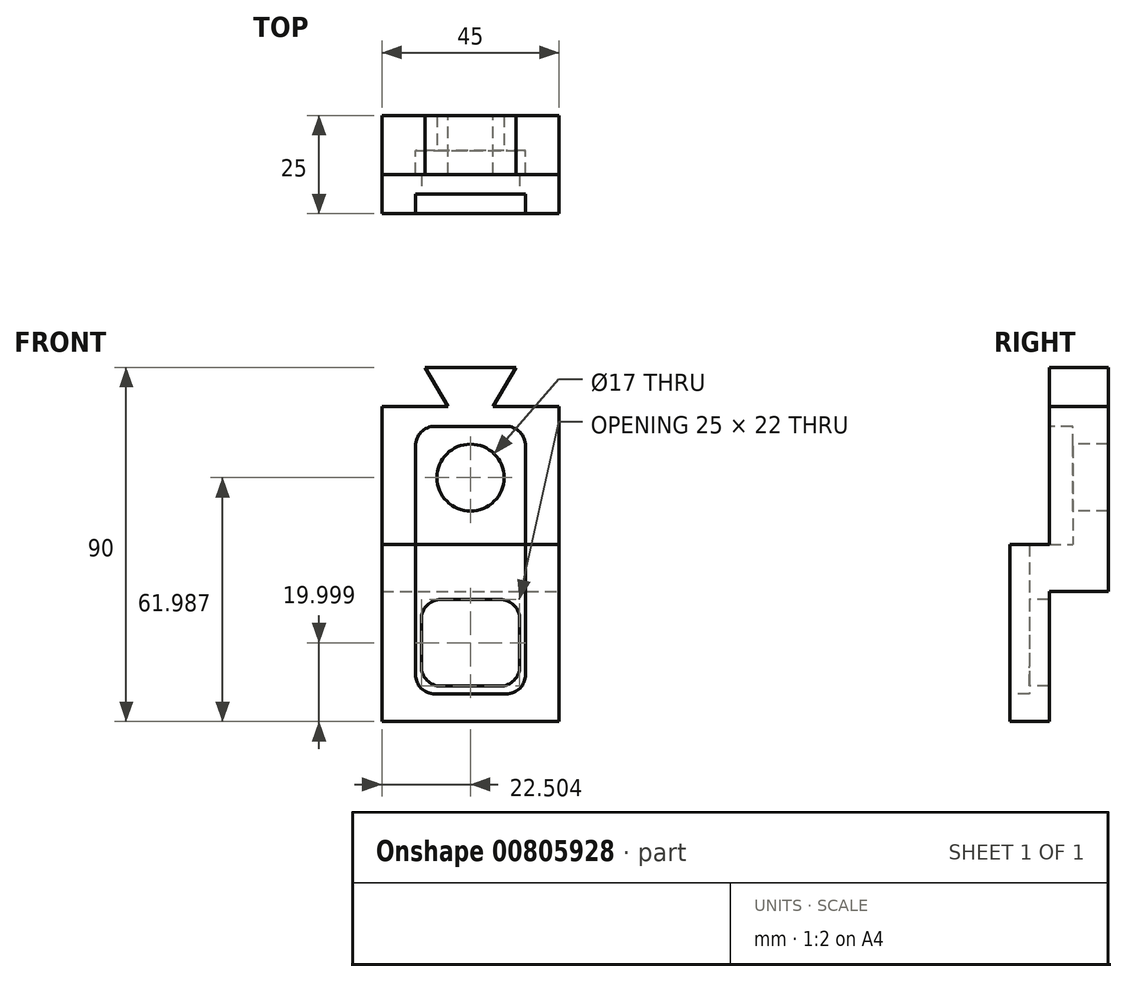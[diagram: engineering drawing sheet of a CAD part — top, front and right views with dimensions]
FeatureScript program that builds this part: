
annotation { "Feature Type Name" : "Feature", "Feature Type Description" : "" }
export const myFeature = defineFeature(function(context is Context, id is Id, definition is map)
    precondition{}
    {
        {
            var Q0;
            Q0=qCreatedBy(makeId("Front.planeOp"),FACE);
            var sketch = newSketch(context, id + "F0", { "sketchPlane" : qUnion([Q0])});
            skLineSegment(sketch, "E0.bottom", {"start": v(-9.42, 1.72) * mm, "end": v(13.58, 1.72) * mm});
            skLineSegment(sketch, "E1", {"start": v(-9.42, 1.72) * mm, "end": v(-3.64, -8.28) * mm});
            skLineSegment(sketch, "E2", {"start": v(7.81, -8.28) * mm, "end": v(13.58, 1.72) * mm});
            skLineSegment(sketch, "E3.bottom", {"start": v(-20.42, -8.28) * mm, "end": v(-3.64, -8.28) * mm});
            skLineSegment(sketch, "E3.top", {"start": v(-20.42, -58.28) * mm, "end": v(24.58, -58.28) * mm});
            skLineSegment(sketch, "E3.left", {"start": v(-20.42, -8.28) * mm, "end": v(-20.42, -58.28) * mm});
            skLineSegment(sketch, "E3.right", {"start": v(24.58, -8.28) * mm, "end": v(24.58, -58.28) * mm});
            skPoint(sketch, "E4.startSnap0", {"position": v(2.08, 1.72) * mm});
            skPoint(sketch, "E4.start.orphan", {"position": v(2.08, 7.05) * mm});
            skLineSegment(sketch, "E5.trimOffspring", {"start": v(7.81, -8.28) * mm, "end": v(24.58, -8.28) * mm});
            skSolve(sketch);
        }
        {
            var Q0;
            Q0=makeQuery(id+"F0.imprint","IMPRINT",FACE,{"disambiguationData":[TD([[makeQuery(id+"F0.imprint","IMPRINT",EDGE,{"derivedFrom":sQuery(id+"F0.wireOp",EDGE,"E0.bottom")}),-1.0]])]});
            extrude(context, id + "F1", {"entities" : qUnion([Q0]), "depth" : 25 * mm, "offsetDistance" : 25 * mm});
        }
        {
            var Q0;
            Q0=makeQuery(id+"F1.opExtrude","CAP_FACE",FACE,{"disambiguationData":[OSD([sQuery(id+"F0.wireOp",EDGE,"E0.bottom"),sQuery(id+"F0.wireOp",EDGE,"E1"),sQuery(id+"F0.wireOp",EDGE,"E2"),sQuery(id+"F0.wireOp",EDGE,"E3.bottom"),sQuery(id+"F0.wireOp",EDGE,"E3.top"),sQuery(id+"F0.wireOp",EDGE,"E3.left"),sQuery(id+"F0.wireOp",EDGE,"E3.right"),sQuery(id+"F0.wireOp",EDGE,"E5.trimOffspring")])],"isStart":false});
            var sketch = newSketch(context, id + "F2", { "sketchPlane" : qUnion([Q0])});
            skCircle(sketch, "E6", {"center": v(2.08, -26.3) * mm, "radius": 8.5 * mm});
            skPoint(sketch, "E6.centerSnap0", {"position": v(2.08, 1.72) * mm});
            skSolve(sketch);
        }
        {
            var Q0;
            Q0=makeQuery(id+"F2.imprint","IMPRINT",FACE,{"disambiguationData":[TD([[makeQuery(id+"F2.imprint","IMPRINT",EDGE,{"derivedFrom":sQuery(id+"F2.wireOp",EDGE,"E6")}),1.0]])]});
            extrude(context, id + "F3", {"entities" : qUnion([Q0]), "operationType" : NewBodyOperationType.REMOVE, "oppositeDirection" : true, "depth" : 25 * mm, "offsetDistance" : 25 * mm});
        }
        {
            var Q0;
            Q0=makeQuery(id+"F1.opExtrude","CAP_FACE",FACE,{"disambiguationData":[OSD([sQuery(id+"F0.wireOp",EDGE,"E0.bottom"),sQuery(id+"F0.wireOp",EDGE,"E1"),sQuery(id+"F0.wireOp",EDGE,"E2"),sQuery(id+"F0.wireOp",EDGE,"E3.bottom"),sQuery(id+"F0.wireOp",EDGE,"E3.top"),sQuery(id+"F0.wireOp",EDGE,"E3.left"),sQuery(id+"F0.wireOp",EDGE,"E3.right"),sQuery(id+"F0.wireOp",EDGE,"E5.trimOffspring")])],"isStart":false});
            var sketch = newSketch(context, id + "F4", { "sketchPlane" : qUnion([Q0])});
            skLineSegment(sketch, "E7.bottom", {"start": v(-6.92, -13.28) * mm, "end": v(11.08, -13.28) * mm});
            skLineSegment(sketch, "E7.top", {"start": v(-11.92, -58.28) * mm, "end": v(16.08, -58.28) * mm});
            skLineSegment(sketch, "E7.left", {"start": v(-11.92, -18.28) * mm, "end": v(-11.92, -58.28) * mm});
            skLineSegment(sketch, "E7.right", {"start": v(16.08, -18.28) * mm, "end": v(16.08, -58.28) * mm});
            skPoint(sketch, "E8.visualSharp", {"position": v(-11.92, -13.28) * mm});
            skArc(sketch, "E8.filletArc", {"start": v(-6.92, -13.28) * mm, "mid": v(-10.45, -14.75) * mm, "end": v(-11.92, -18.28) * mm});
            skPoint(sketch, "E9.visualSharp", {"position": v(16.08, -13.28) * mm});
            skArc(sketch, "E9.filletArc", {"start": v(16.08, -18.28) * mm, "mid": v(14.62, -14.75) * mm, "end": v(11.08, -13.28) * mm});
            skSolve(sketch);
        }
        {
            var Q0;
            Q0 = qSketchRegion(id + "F4", true);
            extrude(context, id + "F5", {"entities" : qUnion([Q0]), "operationType" : NewBodyOperationType.REMOVE, "oppositeDirection" : true, "depth" : 6 * mm, "offsetDistance" : 25 * mm});
        }
        {
            var Q0;
            Q0=makeQuery(id+"F5.boolean.opBoolean","COPY",FACE,{"derivedFrom":makeQuery(id+"F5.opExtrude","CAP_FACE",FACE,{"disambiguationData":[OSD([sQuery(id+"F4.wireOp",EDGE,"E7.bottom"),sQuery(id+"F4.wireOp",EDGE,"E7.top"),sQuery(id+"F4.wireOp",EDGE,"E7.left"),sQuery(id+"F4.wireOp",EDGE,"E7.right"),sQuery(id+"F4.wireOp",EDGE,"E8.filletArc"),sQuery(id+"F4.wireOp",EDGE,"E9.filletArc")])],"isStart":false})});
            var sketch = newSketch(context, id + "F6", { "sketchPlane" : qUnion([Q0])});
            skLineSegment(sketch, "E10.bottom", {"start": v(-11.92, -43.28) * mm, "end": v(16.08, -43.28) * mm});
            skLineSegment(sketch, "E10.top", {"start": v(-11.92, -58.28) * mm, "end": v(16.08, -58.28) * mm});
            skLineSegment(sketch, "E10.left", {"start": v(-11.92, -43.28) * mm, "end": v(-11.92, -58.28) * mm});
            skLineSegment(sketch, "E10.right", {"start": v(16.08, -43.28) * mm, "end": v(16.08, -58.28) * mm});
            skSolve(sketch);
        }
        {
            var Q0;
            Q0=makeQuery(id+"F6.imprint","IMPRINT",FACE,{"disambiguationData":[TD([[makeQuery(id+"F6.imprint","IMPRINT",EDGE,{"derivedFrom":sQuery(id+"F6.wireOp",EDGE,"E10.bottom")}),-1.0]])]});
            extrude(context, id + "F7", {"entities" : qUnion([Q0]), "operationType" : NewBodyOperationType.ADD, "depth" : 6 * mm, "offsetDistance" : 25 * mm});
        }
        {
            var Q0;
            Q0=makeQuery(id+"F7.boolean.opBoolean","MERGE",FACE,{"derivedFrom":[makeQuery(id+"F1.opExtrude","CAP_FACE",FACE,{"disambiguationData":[OSD([sQuery(id+"F0.wireOp",EDGE,"E0.bottom"),sQuery(id+"F0.wireOp",EDGE,"E1"),sQuery(id+"F0.wireOp",EDGE,"E2"),sQuery(id+"F0.wireOp",EDGE,"E3.bottom"),sQuery(id+"F0.wireOp",EDGE,"E3.top"),sQuery(id+"F0.wireOp",EDGE,"E3.left"),sQuery(id+"F0.wireOp",EDGE,"E3.right"),sQuery(id+"F0.wireOp",EDGE,"E5.trimOffspring")])],"isStart":false}),makeQuery(id+"F7.opExtrude","CAP_FACE",FACE,{"disambiguationData":[OSD([sQuery(id+"F6.wireOp",EDGE,"E10.bottom"),sQuery(id+"F6.wireOp",EDGE,"E10.top"),sQuery(id+"F6.wireOp",EDGE,"E10.left"),sQuery(id+"F6.wireOp",EDGE,"E10.right")])],"isStart":false})]});
            var sketch = newSketch(context, id + "F8", { "sketchPlane" : qUnion([Q0])});
            skLineSegment(sketch, "E11.bottom", {"start": v(-20.42, -43.28) * mm, "end": v(24.58, -43.28) * mm});
            skLineSegment(sketch, "E11.top", {"start": v(-20.42, -88.28) * mm, "end": v(24.58, -88.28) * mm});
            skLineSegment(sketch, "E11.left", {"start": v(-20.42, -43.28) * mm, "end": v(-20.42, -88.28) * mm});
            skLineSegment(sketch, "E11.right", {"start": v(24.58, -43.28) * mm, "end": v(24.58, -88.28) * mm});
            skSolve(sketch);
        }
        {
            var Q0;
            {var subQ0=sQuery(id+"F8.wireOp",EDGE,"E11.bottom");var subQ6=sQuery(id+"F4.wireOp",EDGE,"E7.left");var subQ7=makeQuery(id+"F8.imprint","INTERSECT",VERTEX,{"derivedFrom":[makeQuery(id+"F5.boolean.opBoolean","COPY",EDGE,{"derivedFrom":makeQuery(id+"F5.opExtrude","CAP_EDGE",EDGE,{"disambiguationData":[OSD([subQ6])],"isStart":true})}),subQ0]});Q0=makeQuery(id+"F8.imprint","IMPRINT",FACE,{"disambiguationData":[TD([[makeQuery(id+"F8.imprint","IMPRINT",EDGE,{"disambiguationData":[TD([[subQ7,-1.0]])],"derivedFrom":subQ0}),-1.0]])]});}
            var Q1;
            {var subQ0=sQuery(id+"F8.wireOp",EDGE,"E11.top");Q1=makeQuery(id+"F8.imprint","IMPRINT",FACE,{"disambiguationData":[TD([[makeQuery(id+"F8.imprint","IMPRINT",EDGE,{"derivedFrom":subQ0}),1.0]])]});}
            extrude(context, id + "F9", {"entities" : qUnion([Q0, Q1]), "operationType" : NewBodyOperationType.ADD, "depth" : 10 * mm, "offsetDistance" : 25 * mm});
        }
        {
            var Q0;
            Q0=makeQuery(id+"F9.opExtrude","CAP_FACE",FACE,{"disambiguationData":[OSD([sQuery(id+"F8.wireOp",EDGE,"E11.bottom"),sQuery(id+"F8.wireOp",EDGE,"E11.top"),sQuery(id+"F8.wireOp",EDGE,"E11.left"),sQuery(id+"F8.wireOp",EDGE,"E11.right")])],"isStart":false});
            var sketch = newSketch(context, id + "F10", { "sketchPlane" : qUnion([Q0])});
            skLineSegment(sketch, "E12.bottom", {"start": v(-11.92, -43.28) * mm, "end": v(16.08, -43.28) * mm});
            skLineSegment(sketch, "E12.left", {"start": v(-11.92, -43.28) * mm, "end": v(-11.92, -76.28) * mm});
            skLineSegment(sketch, "E12.right", {"start": v(16.08, -43.28) * mm, "end": v(16.08, -76.28) * mm});
            skLineSegment(sketch, "E13", {"start": v(-6.92, -81.28) * mm, "end": v(11.08, -81.28) * mm});
            skPoint(sketch, "E14.visualSharp", {"position": v(-11.92, -81.28) * mm});
            skArc(sketch, "E14.filletArc", {"start": v(-11.92, -76.28) * mm, "mid": v(-10.45, -79.82) * mm, "end": v(-6.92, -81.28) * mm});
            skPoint(sketch, "E15.visualSharp", {"position": v(16.08, -81.28) * mm});
            skArc(sketch, "E15.filletArc", {"start": v(11.08, -81.28) * mm, "mid": v(14.62, -79.82) * mm, "end": v(16.08, -76.28) * mm});
            skSolve(sketch);
        }
        {
            var Q0;
            Q0=makeQuery(id+"F10.imprint","IMPRINT",FACE,{"disambiguationData":[TD([[makeQuery(id+"F10.imprint","IMPRINT",EDGE,{"derivedFrom":sQuery(id+"F10.wireOp",EDGE,"E12.bottom")}),-1.0]])]});
            extrude(context, id + "F11", {"entities" : qUnion([Q0]), "operationType" : NewBodyOperationType.REMOVE, "oppositeDirection" : true, "depth" : 5 * mm, "offsetDistance" : 25 * mm});
        }
        {
            var Q0;
            Q0=makeQuery(id+"F11.boolean.opBoolean","COPY",FACE,{"derivedFrom":makeQuery(id+"F11.opExtrude","CAP_FACE",FACE,{"disambiguationData":[OSD([sQuery(id+"F10.wireOp",EDGE,"E12.bottom"),sQuery(id+"F10.wireOp",EDGE,"E12.left"),sQuery(id+"F10.wireOp",EDGE,"E12.right"),sQuery(id+"F10.wireOp",EDGE,"E13"),sQuery(id+"F10.wireOp",EDGE,"E14.filletArc"),sQuery(id+"F10.wireOp",EDGE,"E15.filletArc")])],"isStart":false})});
            var sketch = newSketch(context, id + "F12", { "sketchPlane" : qUnion([Q0])});
            skLineSegment(sketch, "E16.bottom", {"start": v(9.58, -57.28) * mm, "end": v(-5.42, -57.28) * mm});
            skLineSegment(sketch, "E16.top", {"start": v(9.58, -79.28) * mm, "end": v(-5.42, -79.28) * mm});
            skLineSegment(sketch, "E16.left", {"start": v(14.58, -62.28) * mm, "end": v(14.58, -74.28) * mm});
            skLineSegment(sketch, "E16.right", {"start": v(-10.42, -62.28) * mm, "end": v(-10.42, -74.28) * mm});
            skPoint(sketch, "E17.visualSharp", {"position": v(14.58, -79.28) * mm});
            skArc(sketch, "E17.filletArc", {"start": v(9.58, -79.28) * mm, "mid": v(13.12, -77.82) * mm, "end": v(14.58, -74.28) * mm});
            skPoint(sketch, "E18.visualSharp", {"position": v(-10.42, -79.28) * mm});
            skArc(sketch, "E18.filletArc", {"start": v(-10.42, -74.28) * mm, "mid": v(-8.95, -77.82) * mm, "end": v(-5.42, -79.28) * mm});
            skPoint(sketch, "E19.visualSharp", {"position": v(14.58, -57.28) * mm});
            skArc(sketch, "E19.filletArc", {"start": v(14.58, -62.28) * mm, "mid": v(13.12, -58.75) * mm, "end": v(9.58, -57.28) * mm});
            skPoint(sketch, "E20.visualSharp", {"position": v(-10.42, -57.28) * mm});
            skArc(sketch, "E20.filletArc", {"start": v(-5.42, -57.28) * mm, "mid": v(-8.95, -58.75) * mm, "end": v(-10.42, -62.28) * mm});
            skSolve(sketch);
        }
        {
            var Q0;
            Q0=makeQuery(id+"F7.boolean.opBoolean","MERGE",FACE,{"derivedFrom":[makeQuery(id+"F1.opExtrude","SWEPT_FACE",FACE,{"disambiguationData":[OSD([sQuery(id+"F0.wireOp",EDGE,"E3.top")])]}),makeQuery(id+"F7.opExtrude","SWEPT_FACE",FACE,{"disambiguationData":[OSD([sQuery(id+"F6.wireOp",EDGE,"E10.top")])]})]});
            var sketch = newSketch(context, id + "F13", { "sketchPlane" : qUnion([Q0])});
            skLineSegment(sketch, "E21.bottom", {"start": v(-20.42, 25) * mm, "end": v(24.58, 25) * mm});
            skLineSegment(sketch, "E21.top", {"start": v(-20.42, 0) * mm, "end": v(24.58, 0) * mm});
            skLineSegment(sketch, "E21.left", {"start": v(-20.42, 25) * mm, "end": v(-20.42, 0) * mm});
            skLineSegment(sketch, "E21.right", {"start": v(24.58, 25) * mm, "end": v(24.58, 0) * mm});
            skSolve(sketch);
        }
        {
            var Q0;
            Q0 = qSketchRegion(id + "F13", true);
            extrude(context, id + "F14", {"entities" : qUnion([Q0]), "operationType" : NewBodyOperationType.REMOVE, "oppositeDirection" : true, "depth" : 3 * mm, "offsetDistance" : 25 * mm});
        }
        {
            var Q0;
            Q0=makeQuery(id+"F12.imprint","IMPRINT",FACE,{"disambiguationData":[TD([[makeQuery(id+"F12.imprint","IMPRINT",EDGE,{"derivedFrom":sQuery(id+"F12.wireOp",EDGE,"E16.bottom")}),1.0]])]});
            extrude(context, id + "F15", {"entities" : qUnion([Q0]), "operationType" : NewBodyOperationType.REMOVE, "oppositeDirection" : true, "depth" : 25 * mm, "offsetDistance" : 25 * mm});
        }
        {
            var Q0;
            Q0=makeQuery(id+"F1.opExtrude","CAP_FACE",FACE,{"disambiguationData":[OSD([sQuery(id+"F0.wireOp",EDGE,"E0.bottom"),sQuery(id+"F0.wireOp",EDGE,"E1"),sQuery(id+"F0.wireOp",EDGE,"E2"),sQuery(id+"F0.wireOp",EDGE,"E3.bottom"),sQuery(id+"F0.wireOp",EDGE,"E3.top"),sQuery(id+"F0.wireOp",EDGE,"E3.left"),sQuery(id+"F0.wireOp",EDGE,"E3.right"),sQuery(id+"F0.wireOp",EDGE,"E5.trimOffspring")])],"isStart":true});
            var sketch = newSketch(context, id + "F16", { "sketchPlane" : qUnion([Q0])});
            skLineSegment(sketch, "E22.bottom", {"start": v(-24.58, -8.28) * mm, "end": v(20.42, -8.28) * mm});
            skLineSegment(sketch, "E22.top", {"start": v(-24.58, -55.28) * mm, "end": v(20.42, -55.28) * mm});
            skLineSegment(sketch, "E22.left", {"start": v(-24.58, -8.28) * mm, "end": v(-24.58, -55.28) * mm});
            skLineSegment(sketch, "E22.right", {"start": v(20.42, -8.28) * mm, "end": v(20.42, -55.28) * mm});
            skSolve(sketch);
        }
        {
            var Q0;
            Q0 = qSketchRegion(id + "F16", true);
            extrude(context, id + "F17", {"entities" : qUnion([Q0]), "operationType" : NewBodyOperationType.REMOVE, "oppositeDirection" : true, "depth" : 10 * mm, "offsetDistance" : 25 * mm});
        }
        {
            var Q0;
            Q0=makeQuery(id+"F1.opExtrude","CAP_FACE",FACE,{"disambiguationData":[OSD([sQuery(id+"F0.wireOp",EDGE,"E0.bottom"),sQuery(id+"F0.wireOp",EDGE,"E1"),sQuery(id+"F0.wireOp",EDGE,"E2"),sQuery(id+"F0.wireOp",EDGE,"E3.bottom"),sQuery(id+"F0.wireOp",EDGE,"E3.top"),sQuery(id+"F0.wireOp",EDGE,"E3.left"),sQuery(id+"F0.wireOp",EDGE,"E3.right"),sQuery(id+"F0.wireOp",EDGE,"E5.trimOffspring")])],"isStart":true});
            var sketch = newSketch(context, id + "F18", { "sketchPlane" : qUnion([Q0])});
            skLineSegment(sketch, "E23", {"start": v(-13.58, 1.72) * mm, "end": v(-7.81, -8.28) * mm});
            skLineSegment(sketch, "E24", {"start": v(-7.81, -8.28) * mm, "end": v(3.64, -8.28) * mm});
            skLineSegment(sketch, "E25", {"start": v(3.64, -8.28) * mm, "end": v(9.42, 1.72) * mm});
            skLineSegment(sketch, "E26", {"start": v(9.42, 1.72) * mm, "end": v(-13.58, 1.72) * mm});
            skSolve(sketch);
        }
        {
            var Q0;
            Q0 = qSketchRegion(id + "F18", true);
            extrude(context, id + "F19", {"entities" : qUnion([Q0]), "operationType" : NewBodyOperationType.REMOVE, "oppositeDirection" : true, "depth" : 10 * mm, "offsetDistance" : 25 * mm});
        }
    });
